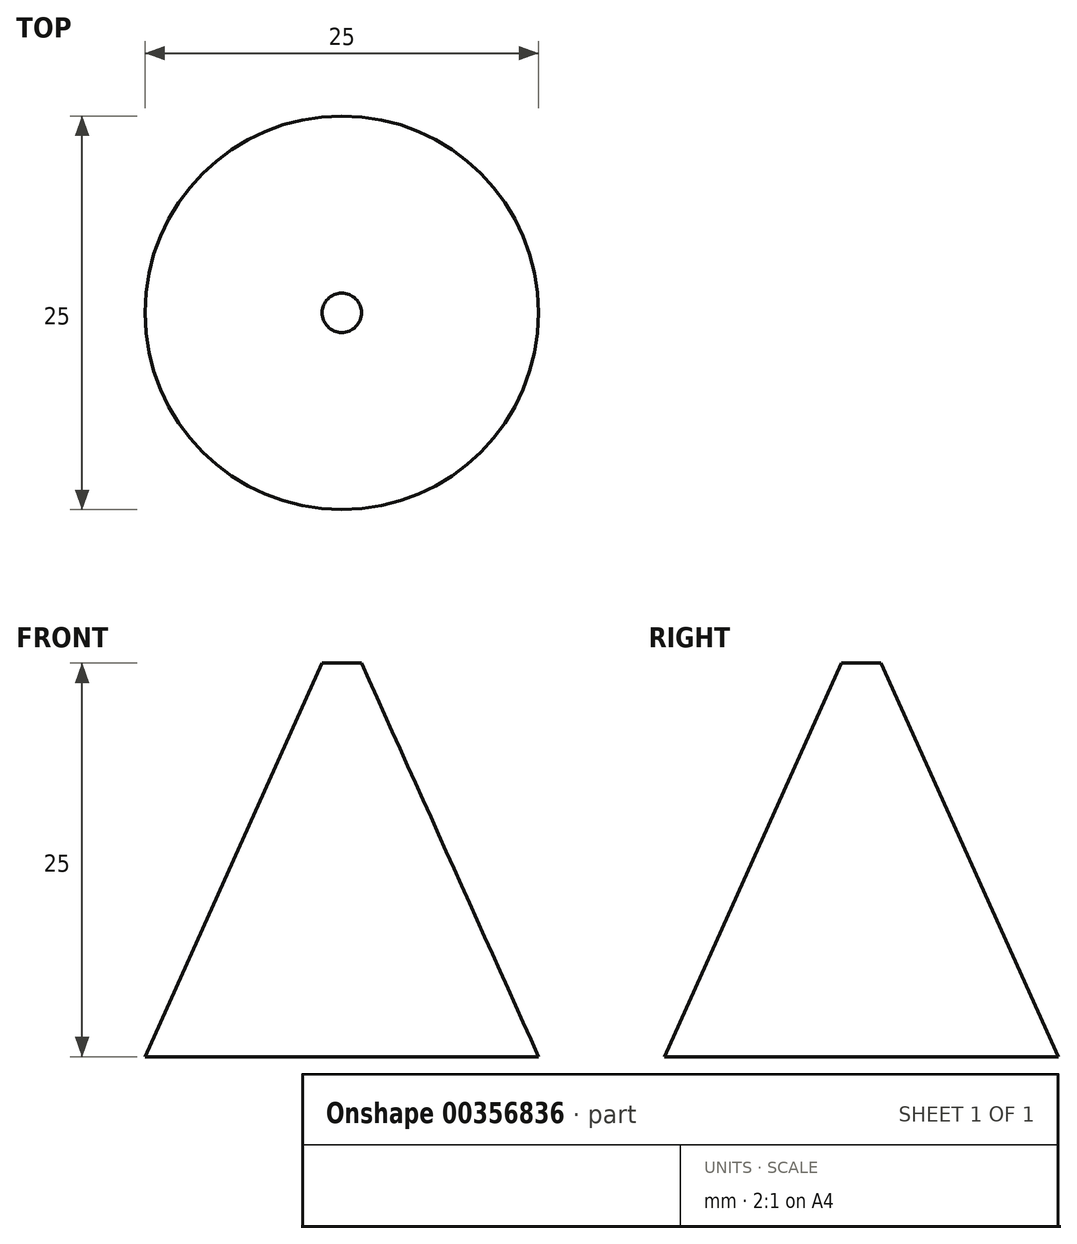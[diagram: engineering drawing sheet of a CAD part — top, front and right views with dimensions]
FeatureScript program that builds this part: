
annotation { "Feature Type Name" : "Feature", "Feature Type Description" : "" }
export const myFeature = defineFeature(function(context is Context, id is Id, definition is map)
    precondition{}
    {
        {
            assignVariable(context, id + "F0", {"name" : "Size", "anyValue" : 25});
        }
        {
            var Q0;
            Q0=qCreatedBy(makeId("Top.planeOp"),FACE);
            cPlane(context, id + "F1", {"entities" : qUnion([Q0]), "cplaneType" : CPlaneType.OFFSET, "offset" : (getVariable(context, 'Size')) * mm, "width" : 150 * mm, "height" : 150 * mm});
        }
        {
            var Q0;
            Q0=qCreatedBy(makeId("Top.planeOp"),FACE);
            var sketch = newSketch(context, id + "F2", { "sketchPlane" : qUnion([Q0])});
            skCircle(sketch, "E0", {"center": v(0, 0) * mm, "radius": 12.5 * mm});
            skSolve(sketch);
        }
        {
            var Q0;
            Q0=qCreatedBy(id+"F1.planeOp",FACE);
            var sketch = newSketch(context, id + "F3", { "sketchPlane" : qUnion([Q0])});
            skCircle(sketch, "E1", {"center": v(0, 0) * mm, "radius": 1.25 * mm});
            skSolve(sketch);
        }
        {
            var Q0;
            Q0=makeQuery(id+"F2.imprint","IMPRINT",FACE,{"disambiguationData":[TD([[makeQuery(id+"F2.imprint","IMPRINT",EDGE,{"derivedFrom":sQuery(id+"F2.wireOp",EDGE,"E0")}),1.0]])]});
            var Q1;
            Q1=makeQuery(id+"F3.imprint","IMPRINT",FACE,{"disambiguationData":[TD([[makeQuery(id+"F3.imprint","IMPRINT",EDGE,{"derivedFrom":sQuery(id+"F3.wireOp",EDGE,"E1")}),1.0]])]});
            loft(context, id + "F4", {"sheetProfilesArray" : [{ "sheetProfileEntities" : qUnion([Q0]) }, { "sheetProfileEntities" : qUnion([Q1]) }]});
        }
    });
